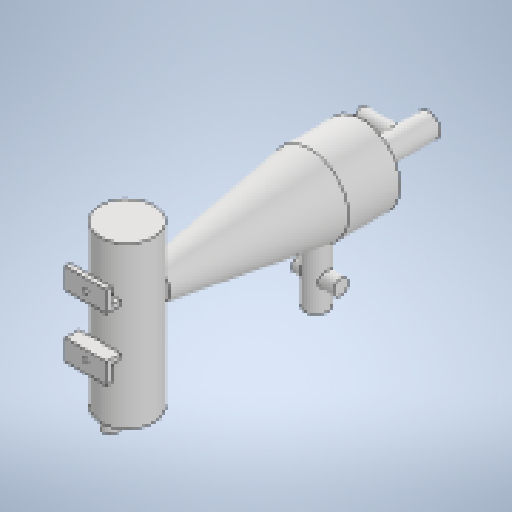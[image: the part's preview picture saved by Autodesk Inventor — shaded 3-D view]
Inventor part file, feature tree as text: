
AUTODESK INVENTOR PART (.ipt)
format: ipt  version: 2025.3 (Build 293356030, 356C)  size: 333,824 bytes
history: native  units: mm
features: sketch x7, extrude x6, projected_geometry x5, revolve x1
ambient origin geometry x8: Origin, YZ Plane, XZ Plane, XY Plane, X Axis, Y Axis, Z Axis, Center Point
bodies: Solid1 (feature_tree)
feature tree (19):
  extrude  "Extrusion1"  Depth=130.0mm TaperAngle=0.0deg
  revolve  "Revolution1"  [1 undecoded]
  extrude  "Extrusion2"  Depth=130.0mm
  sketch  "Sketch4"  dims[d10=150.0mm d11=30.0mm]
  extrude  "Extrusion3"  Depth=30.0mm
  extrude  "Extrusion4"  TaperAngle=90.0deg  [1 undecoded]
  extrude  "Extrusion5"  Depth=10.0mm
  extrude  "Extrusion6"  Depth=10.0mm
  sketch  "Sketch1"  dims[d0=105.0mm d1=130.0mm d2=180.0mm d3=0.0mm d4=0.0mm]
  sketch  "Sketch2"  dims[d5=80.0mm d6=530.0mm]
  sketch  "Sketch3"  dims[d8=45.0mm d9=130.0mm]
  projected_geometry  "Projected Loop1"
  projected_geometry  "Projected Loop2"
  sketch  "Sketch5"  dims[d12=100.0mm d13=90.0deg]
  projected_geometry  "Projected Loop3"
  sketch  "Sketch6"  dims[d14=95.0mm d15=10.0mm]
  sketch  "Sketch7"  dims[d16=10.0mm d17=10.0mm d18=80.0mm d19=40.0mm d20=160.0mm d21=80.0mm d22=0.0mm d23=115.0mm d24=10.0mm d25=45.0mm d26=47.167616mm d27=40.0mm d28=240.0mm d29=0.0mm d30=30.0mm d31=20.0mm d32=0.0mm d33=30.0mm d34=30.0mm d35=80.0mm d36=0.0mm d37=10.0mm d38=0.0mm]
  projected_geometry  "Projected Loop4"
  projected_geometry  "Projected Loop5"
note: 2 required parameter values undecoded (feature->parameter linkage not recoverable at this tier; creation-order binding heuristic only, values carry confidence <= 0.55)